# Revit family: BuroSeating_Konfurb Studio
name_source: partatom
category: Furniture
units: mm (PartAtom-declared; Revit-internal decimal feet)

## family parameters
Always vertical = Yes
Cut with Voids When Loaded = No
OmniClass Number = 23.40.70.14.64.11
OmniClass Title = Office Furniture
Room Calculation Point = No
Shared = No
Work Plane-Based = No

## types (3) — shared parameters
Assembly Code = E2020
BaseFrameMaterial = BuroSeating_Fabric_Augustus Aegean
BaseHeight = 18 mm  [stored 0.0590551 ft]
FeetDiameter = 50 mm  [stored 0.164042 ft]
Manufacturer = Buro Seating
NominalDepth = 745 mm  [stored 2.44423 ft]
NominalHeight = 1350 mm  [stored 4.42913 ft]
ProductGroup = Konfurb Studio
ProductPageURL AU = https://buroseating.com
ProductPageURL NZ = https://buroseating.co.nz
ProductRange = Konfurb
SeatHeight = 450 mm  [stored 1.47638 ft]
URL = https://buroseating.co.nz
URL AU = https://buroseating.com
WarrantyDescription = Full 5 year guarantee (excluding upholstery)
zero-valued in all types: Default Elevation

## per-type parameters (varying)
| type | CushionArray | Description | FeetMaterial | Model | NominalLength | calc_CushionArray |
| 1 Seater | 2 | Konfurb Studio 1 Seater | BuroSeating_Plastic_Black | KON565 | 790 mm  [stored 2.59186 ft] | 2 |
| 2 Seater | 2 | Konfurb Studio 2 Seater | BuroSeating_Fabric_Augustus Aegean | KON564 | 1450 mm  [stored 4.75722 ft] | 2 |
| 3 Seater | 3 | Konfurb Studio 3 Seater | BuroSeating_Fabric_Augustus Aegean | KON566 | 2110 mm  [stored 6.92257 ft] | 3 |

note: [stored X ft] marks values corroborated as IEEE doubles in the binary element streams (Revit-internal decimal feet)

## geometry (parser evidence)
native form markers: Sweep x5
no freeform markers — native parametric forms only
